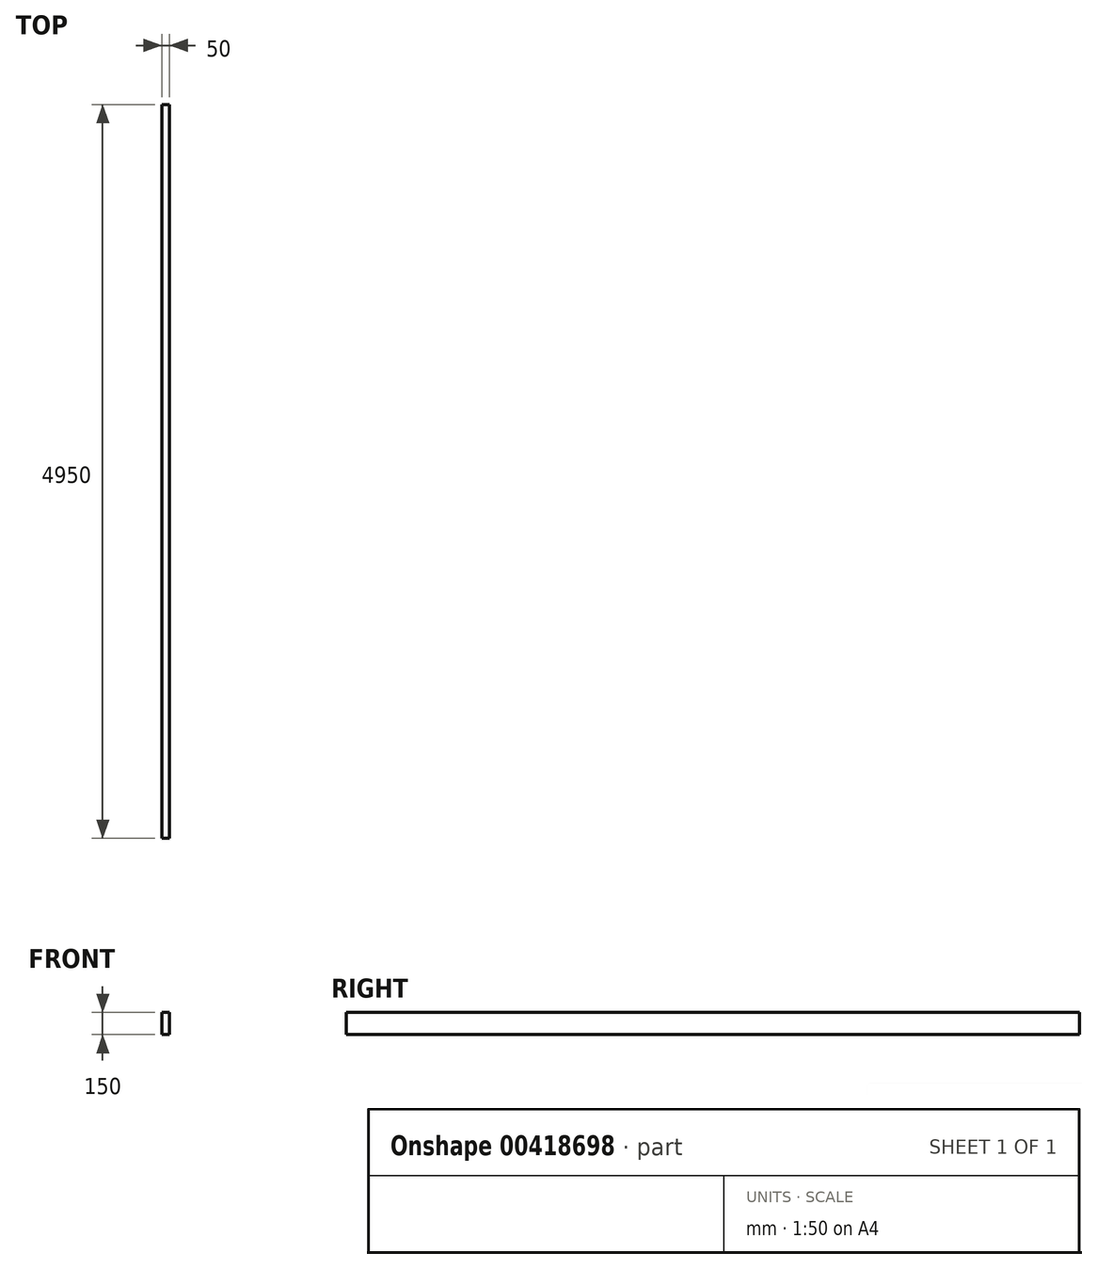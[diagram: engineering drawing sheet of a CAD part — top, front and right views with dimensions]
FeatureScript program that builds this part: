
annotation { "Feature Type Name" : "Feature", "Feature Type Description" : "" }
export const myFeature = defineFeature(function(context is Context, id is Id, definition is map)
    precondition{}
    {
        {
            var Q0;
            Q0=qCreatedBy(makeId("Front.planeOp"),FACE);
            var sketch = newSketch(context, id + "F0", { "sketchPlane" : qUnion([Q0])});
            skLineSegment(sketch, "E0.bottom", {"start": v(25, 75) * mm, "end": v(-25, 75) * mm});
            skLineSegment(sketch, "E0.top", {"start": v(25, -75) * mm, "end": v(-25, -75) * mm});
            skLineSegment(sketch, "E0.left", {"start": v(25, 75) * mm, "end": v(25, -75) * mm});
            skLineSegment(sketch, "E0.right", {"start": v(-25, 75) * mm, "end": v(-25, -75) * mm});
            skPoint(sketch, "E0.middle", {"position": v(0, 0) * mm});
            skSolve(sketch);
        }
        {
            var Q0;
            Q0 = qSketchRegion(id + "F0", true);
            extrude(context, id + "F1", {"entities" : qUnion([Q0]), "endBound" : BoundingType.SYMMETRIC, "depth" : 4950 * mm});
        }
    });
